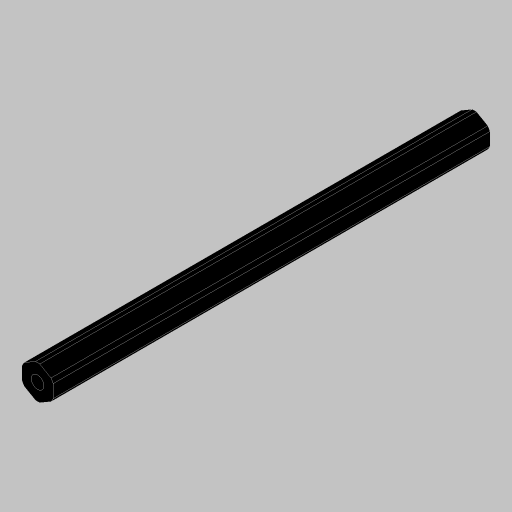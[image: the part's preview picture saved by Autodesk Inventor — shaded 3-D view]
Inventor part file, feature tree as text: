
AUTODESK INVENTOR PART (.ipt)
format: ipt  version: 2023.5 (Build 275446000, 446)  size: 115,712 bytes
history: native  units: in
note: dims shown in document units (in); Inventor stores cm internally (conversion verified against a paired STEP export)
features: extrude x2, projected_geometry x2, hole x1
ambient origin geometry x8: Origin, YZ Plane, XZ Plane, XY Plane, X Axis, Y Axis, Z Axis, Center Point
bodies: Solid1 (feature_tree)
feature tree (5):
  extrude  "Extrusion1"  TaperAngle=0.0deg  [1 undecoded]
  hole  "Hole1"  [1 undecoded]
  extrude  "Extrusion3"  TaperAngle=0.0deg  [1 undecoded]
  projected_geometry  "Project Cut Edges1"
  projected_geometry  "Project Cut Edges2"
note: 3 required parameter values undecoded (feature->parameter linkage not recoverable at this tier; creation-order binding heuristic only, values carry confidence <= 0.55)
